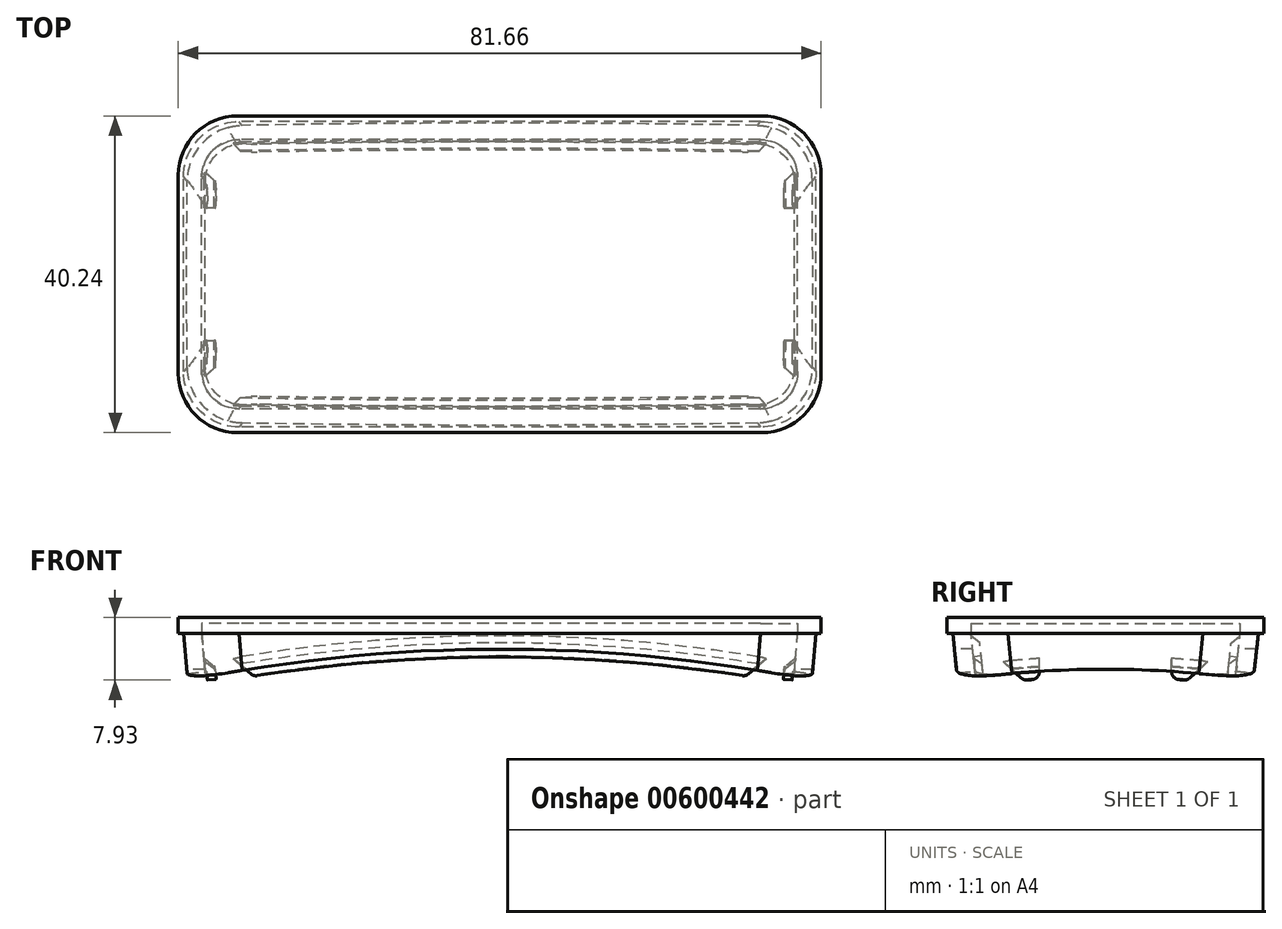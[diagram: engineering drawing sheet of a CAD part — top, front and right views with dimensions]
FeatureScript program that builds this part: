
annotation { "Feature Type Name" : "Feature", "Feature Type Description" : "" }
export const myFeature = defineFeature(function(context is Context, id is Id, definition is map)
    precondition{}
    {
        {
            var Q0;
            Q0=qCreatedBy(makeId("Top.planeOp"),FACE);
            var sketch = newSketch(context, id + "F0", { "sketchPlane" : qUnion([Q0])});
            skLineSegment(sketch, "E0.bottom", {"start": v(-32.64, 18.78) * mm, "end": v(32.64, 18.78) * mm});
            skLineSegment(sketch, "E0.top", {"start": v(-32.64, -18.78) * mm, "end": v(32.64, -18.78) * mm});
            skLineSegment(sketch, "E0.left", {"start": v(-39.64, 11.78) * mm, "end": v(-39.64, -11.78) * mm});
            skLineSegment(sketch, "E0.right", {"start": v(39.64, 11.78) * mm, "end": v(39.64, -11.78) * mm});
            skPoint(sketch, "E0.middle", {"position": v(0, 0) * mm});
            skPoint(sketch, "E1.visualSharp", {"position": v(-39.64, 18.78) * mm});
            skArc(sketch, "E1.filletArc", {"start": v(-32.64, 18.78) * mm, "mid": v(-37.59, 16.73) * mm, "end": v(-39.64, 11.78) * mm});
            skPoint(sketch, "E2.visualSharp", {"position": v(39.64, 18.78) * mm});
            skArc(sketch, "E2.filletArc", {"start": v(39.64, 11.78) * mm, "mid": v(37.59, 16.73) * mm, "end": v(32.64, 18.78) * mm});
            skPoint(sketch, "E3.visualSharp", {"position": v(39.64, -18.78) * mm});
            skArc(sketch, "E3.filletArc", {"start": v(32.64, -18.78) * mm, "mid": v(37.59, -16.73) * mm, "end": v(39.64, -11.78) * mm});
            skPoint(sketch, "E4.visualSharp", {"position": v(-39.64, -18.78) * mm});
            skArc(sketch, "E4.filletArc", {"start": v(-39.64, -11.78) * mm, "mid": v(-37.59, -16.73) * mm, "end": v(-32.64, -18.78) * mm});
            skSolve(sketch);
        }
        {
            var Q0;
            Q0=qCreatedBy(makeId("Top.planeOp"),FACE);
            cPlane(context, id + "F1", {"entities" : qUnion([Q0]), "cplaneType" : CPlaneType.OFFSET, "offset" : 100 * mm, "width" : 150 * mm, "height" : 150 * mm});
        }
        {
            var Q0;
            Q0=qCreatedBy(id+"F1.planeOp",FACE);
            var sketch = newSketch(context, id + "F2", { "sketchPlane" : qUnion([Q0])});
            skLineSegment(sketch, "E5.bottom", {"start": v(-40.98, 29.29) * mm, "end": v(40.98, 29.29) * mm});
            skLineSegment(sketch, "E5.top", {"start": v(-40.98, -29.29) * mm, "end": v(40.98, -29.29) * mm});
            skLineSegment(sketch, "E5.left", {"start": v(-48.38, 21.9) * mm, "end": v(-48.38, -21.9) * mm});
            skLineSegment(sketch, "E5.right", {"start": v(48.38, 21.9) * mm, "end": v(48.38, -21.9) * mm});
            skPoint(sketch, "E5.middle", {"position": v(0, 0) * mm});
            skPoint(sketch, "E6.visualSharp", {"position": v(-48.38, 29.29) * mm});
            skArc(sketch, "E6.filletArc", {"start": v(-40.98, 29.29) * mm, "mid": v(-46.22, 27.12) * mm, "end": v(-48.38, 21.9) * mm});
            skPoint(sketch, "E7.visualSharp", {"position": v(48.38, 29.29) * mm});
            skArc(sketch, "E7.filletArc", {"start": v(48.38, 21.9) * mm, "mid": v(46.22, 27.12) * mm, "end": v(40.98, 29.29) * mm});
            skPoint(sketch, "E8.visualSharp", {"position": v(48.38, -29.3) * mm});
            skArc(sketch, "E8.filletArc", {"start": v(40.98, -29.29) * mm, "mid": v(46.22, -27.12) * mm, "end": v(48.38, -21.9) * mm});
            skPoint(sketch, "E9.visualSharp", {"position": v(-48.38, -29.3) * mm});
            skArc(sketch, "E9.filletArc", {"start": v(-48.38, -21.9) * mm, "mid": v(-46.22, -27.12) * mm, "end": v(-40.98, -29.29) * mm});
            skSolve(sketch);
        }
        {
            var Q0;
            Q0=makeQuery(id+"F0.imprint","IMPRINT",FACE,{"disambiguationData":[TD([[makeQuery(id+"F0.imprint","IMPRINT",EDGE,{"derivedFrom":sQuery(id+"F0.wireOp",EDGE,"E0.bottom")}),-1.0]])]});
            var Q1;
            Q1=makeQuery(id+"F2.imprint","IMPRINT",FACE,{"disambiguationData":[TD([[makeQuery(id+"F2.imprint","IMPRINT",EDGE,{"derivedFrom":sQuery(id+"F2.wireOp",EDGE,"E5.bottom")}),-1.0]])]});
            loft(context, id + "F3", {"sheetProfilesArray" : [{ "sheetProfileEntities" : qUnion([Q0]) }, { "sheetProfileEntities" : qUnion([Q1]) }]});
        }
        {
            var Q0;
            Q0=makeQuery(id+"F3.opLoft","CAP_FACE",FACE,{"disambiguationData":[OSD([makeQuery(id+"F0.imprint","IMPRINT",FACE,{"disambiguationData":[TD([[makeQuery(id+"F0.imprint","IMPRINT",EDGE,{"derivedFrom":sQuery(id+"F0.wireOp",EDGE,"E0.bottom")}),-1.0]])]})])],"isStart":true});
            var Q1;
            Q1=makeQuery(id+"F3.opLoft","CAP_FACE",FACE,{"disambiguationData":[OSD([makeQuery(id+"F2.imprint","IMPRINT",FACE,{"disambiguationData":[TD([[makeQuery(id+"F2.imprint","IMPRINT",EDGE,{"derivedFrom":sQuery(id+"F2.wireOp",EDGE,"E5.bottom")}),-1.0]])]})])],"isStart":true});
            shell(context, id + "F4", {"entities" : qUnion([Q0, Q1]), "thickness" : 2.3 * mm});
        }
        {
            var Q0;
            Q0=qCreatedBy(makeId("Front.planeOp"),FACE);
            var sketch = newSketch(context, id + "F5", { "sketchPlane" : qUnion([Q0])});
            skArc(sketch, "E10", {"start": v(39.64, 0) * mm, "mid": v(0, 3.97) * mm, "end": v(-39.64, 0) * mm});
            skLineSegment(sketch, "E11", {"start": v(-39.64, 0) * mm, "end": v(39.64, 0) * mm});
            skSolve(sketch);
        }
        {
            var Q0;
            Q0 = qSketchRegion(id + "F5", true);
            var Q1;
            Q1=makeQuery(id+"F3.opLoft","SWEPT_FACE",FACE,{"disambiguationData":[OSD([sQuery(id+"F0.wireOp",EDGE,"E0.bottom"),sQuery(id+"F0.wireOp",EDGE,"E1.filletArc"),sQuery(id+"F0.wireOp",EDGE,"E2.filletArc"),sQuery(id+"F2.wireOp",EDGE,"E5.bottom"),sQuery(id+"F2.wireOp",EDGE,"E6.filletArc"),sQuery(id+"F2.wireOp",EDGE,"E7.filletArc")])]});
            var Q2;
            Q2=makeQuery(id+"F3.opLoft","SWEPT_FACE",FACE,{"disambiguationData":[OSD([sQuery(id+"F0.wireOp",EDGE,"E0.top"),sQuery(id+"F0.wireOp",EDGE,"E3.filletArc"),sQuery(id+"F0.wireOp",EDGE,"E4.filletArc"),sQuery(id+"F2.wireOp",EDGE,"E5.top"),sQuery(id+"F2.wireOp",EDGE,"E8.filletArc"),sQuery(id+"F2.wireOp",EDGE,"E9.filletArc")])]});
            extrude(context, id + "F6", {"entities" : qUnion([Q0]), "operationType" : NewBodyOperationType.REMOVE, "endBound" : BoundingType.UP_TO_SURFACE, "oppositeDirection" : true, "depth" : 25 * mm, "endBoundEntityFace" : qUnion([Q1]), "offsetDistance" : 25 * mm, "hasSecondDirection" : true, "secondDirectionBound" : SecondDirectionBoundingType.UP_TO_SURFACE, "secondDirectionOppositeDirection" : false, "secondDirectionDepth" : 25 * mm, "secondDirectionBoundEntityFace" : qUnion([Q2])});
        }
        {
            var Q0;
            Q0=qCreatedBy(makeId("Right.planeOp"),FACE);
            var sketch = newSketch(context, id + "F7", { "sketchPlane" : qUnion([Q0])});
            skArc(sketch, "E12", {"start": v(18.78, 0) * mm, "mid": v(0, 1.42) * mm, "end": v(-18.78, 0) * mm});
            skLineSegment(sketch, "E13", {"start": v(-18.78, 0) * mm, "end": v(18.78, 0) * mm});
            skSolve(sketch);
        }
        {
            var Q0;
            Q0 = qSketchRegion(id + "F7", true);
            var Q1;
            Q1=makeQuery(id+"F3.opLoft","SWEPT_FACE",FACE,{"disambiguationData":[OSD([sQuery(id+"F0.wireOp",EDGE,"E0.right"),sQuery(id+"F0.wireOp",EDGE,"E2.filletArc"),sQuery(id+"F0.wireOp",EDGE,"E3.filletArc"),sQuery(id+"F2.wireOp",EDGE,"E5.right"),sQuery(id+"F2.wireOp",EDGE,"E7.filletArc"),sQuery(id+"F2.wireOp",EDGE,"E8.filletArc")])]});
            var Q2;
            Q2=makeQuery(id+"F3.opLoft","SWEPT_FACE",FACE,{"disambiguationData":[OSD([sQuery(id+"F0.wireOp",EDGE,"E0.left"),sQuery(id+"F0.wireOp",EDGE,"E1.filletArc"),sQuery(id+"F0.wireOp",EDGE,"E4.filletArc"),sQuery(id+"F2.wireOp",EDGE,"E5.left"),sQuery(id+"F2.wireOp",EDGE,"E6.filletArc"),sQuery(id+"F2.wireOp",EDGE,"E9.filletArc")])]});
            extrude(context, id + "F8", {"entities" : qUnion([Q0]), "operationType" : NewBodyOperationType.REMOVE, "endBound" : BoundingType.UP_TO_SURFACE, "depth" : 25 * mm, "endBoundEntityFace" : qUnion([Q1]), "offsetDistance" : 25 * mm, "hasSecondDirection" : true, "secondDirectionBound" : SecondDirectionBoundingType.UP_TO_SURFACE, "secondDirectionOppositeDirection" : true, "secondDirectionDepth" : 25 * mm, "secondDirectionBoundEntityFace" : qUnion([Q2])});
        }
        {
            var Q0;
            Q0=makeQuery(id+"F8.boolean.opBoolean","INTERSECT",EDGE,{"disambiguationData":[OD(2.0)],"derivedFrom":[makeQuery(id+"F6.boolean.opBoolean","COPY",FACE,{"derivedFrom":makeQuery(id+"F6.opExtrude","SWEPT_FACE",FACE,{"disambiguationData":[OSD([sQuery(id+"F5.wireOp",EDGE,"E10")])]})}),makeQuery(id+"F8.opExtrude","SWEPT_FACE",FACE,{"disambiguationData":[OSD([sQuery(id+"F7.wireOp",EDGE,"E12")])]})]});
            var Q1;
            Q1=makeQuery(id+"F8.boolean.opBoolean","INTERSECT",EDGE,{"disambiguationData":[OD(3.0)],"derivedFrom":[makeQuery(id+"F6.boolean.opBoolean","COPY",FACE,{"derivedFrom":makeQuery(id+"F6.opExtrude","SWEPT_FACE",FACE,{"disambiguationData":[OSD([sQuery(id+"F5.wireOp",EDGE,"E10")])]})}),makeQuery(id+"F8.opExtrude","SWEPT_FACE",FACE,{"disambiguationData":[OSD([sQuery(id+"F7.wireOp",EDGE,"E12")])]})]});
            var Q2;
            Q2=makeQuery(id+"F8.boolean.opBoolean","INTERSECT",EDGE,{"disambiguationData":[OD(0.0)],"derivedFrom":[makeQuery(id+"F6.boolean.opBoolean","COPY",FACE,{"derivedFrom":makeQuery(id+"F6.opExtrude","SWEPT_FACE",FACE,{"disambiguationData":[OSD([sQuery(id+"F5.wireOp",EDGE,"E10")])]})}),makeQuery(id+"F8.opExtrude","SWEPT_FACE",FACE,{"disambiguationData":[OSD([sQuery(id+"F7.wireOp",EDGE,"E12")])]})]});
            var Q3;
            Q3=makeQuery(id+"F8.boolean.opBoolean","INTERSECT",EDGE,{"disambiguationData":[OD(1.0)],"derivedFrom":[makeQuery(id+"F6.boolean.opBoolean","COPY",FACE,{"derivedFrom":makeQuery(id+"F6.opExtrude","SWEPT_FACE",FACE,{"disambiguationData":[OSD([sQuery(id+"F5.wireOp",EDGE,"E10")])]})}),makeQuery(id+"F8.opExtrude","SWEPT_FACE",FACE,{"disambiguationData":[OSD([sQuery(id+"F7.wireOp",EDGE,"E12")])]})]});
            fillet(context, id + "F9", {"entities" : qUnion([Q0, Q1, Q2, Q3]), "radius" : 40 * mm, "tangentPropagation" : true, "allowEdgeOverflow" : false});
        }
        {
            var Q0;
            Q0=qCreatedBy(makeId("Front.planeOp"),FACE);
            var sketch = newSketch(context, id + "F10", { "sketchPlane" : qUnion([Q0])});
            skLineSegment(sketch, "E14.bottom", {"start": v(-48.38, 100) * mm, "end": v(48.38, 100) * mm});
            skLineSegment(sketch, "E14.top", {"start": v(-48.38, 7.97) * mm, "end": v(48.38, 7.97) * mm});
            skLineSegment(sketch, "E14.left", {"start": v(-48.38, 100) * mm, "end": v(-48.38, 7.97) * mm});
            skLineSegment(sketch, "E14.right", {"start": v(48.38, 100) * mm, "end": v(48.38, 7.97) * mm});
            skSolve(sketch);
        }
        {
            var Q0;
            Q0 = qSketchRegion(id + "F10", true);
            var Q1;
            Q1=makeQuery(id+"F3.opLoft","SWEPT_FACE",FACE,{"disambiguationData":[OSD([sQuery(id+"F0.wireOp",EDGE,"E0.bottom"),sQuery(id+"F0.wireOp",EDGE,"E1.filletArc"),sQuery(id+"F0.wireOp",EDGE,"E2.filletArc"),sQuery(id+"F2.wireOp",EDGE,"E5.bottom"),sQuery(id+"F2.wireOp",EDGE,"E6.filletArc"),sQuery(id+"F2.wireOp",EDGE,"E7.filletArc")])]});
            var Q2;
            Q2=makeQuery(id+"F3.opLoft","SWEPT_FACE",FACE,{"disambiguationData":[OSD([sQuery(id+"F0.wireOp",EDGE,"E0.top"),sQuery(id+"F0.wireOp",EDGE,"E3.filletArc"),sQuery(id+"F0.wireOp",EDGE,"E4.filletArc"),sQuery(id+"F2.wireOp",EDGE,"E5.top"),sQuery(id+"F2.wireOp",EDGE,"E8.filletArc"),sQuery(id+"F2.wireOp",EDGE,"E9.filletArc")])]});
            extrude(context, id + "F11", {"entities" : qUnion([Q0]), "operationType" : NewBodyOperationType.REMOVE, "endBound" : BoundingType.UP_TO_SURFACE, "oppositeDirection" : true, "depth" : 25 * mm, "endBoundEntityFace" : qUnion([Q1]), "offsetDistance" : 25 * mm, "hasSecondDirection" : true, "secondDirectionBound" : SecondDirectionBoundingType.UP_TO_SURFACE, "secondDirectionOppositeDirection" : false, "secondDirectionDepth" : 25 * mm, "secondDirectionBoundEntityFace" : qUnion([Q2])});
        }
        {
            var Q0;
            Q0=makeQuery(id+"F4.opShell","OFFSET_FACE",FACE,{"disambiguationData":[OSD([sQuery(id+"F0.wireOp",EDGE,"E0.bottom"),sQuery(id+"F0.wireOp",EDGE,"E1.filletArc"),sQuery(id+"F0.wireOp",EDGE,"E2.filletArc"),sQuery(id+"F2.wireOp",EDGE,"E5.bottom"),sQuery(id+"F2.wireOp",EDGE,"E6.filletArc"),sQuery(id+"F2.wireOp",EDGE,"E7.filletArc")])]});
            var sketch = newSketch(context, id + "F12", { "sketchPlane" : qUnion([Q0])});
            skArc(sketch, "E15", {"start": v(32.77, 3.53) * mm, "mid": v(0, 6.2) * mm, "end": v(-32.77, 3.53) * mm});
            skLineSegment(sketch, "E16", {"start": v(31.27, 2.25) * mm, "end": v(32.77, 3.53) * mm});
            skArc(sketch, "E17", {"start": v(31.27, 2.25) * mm, "mid": v(0, 4.7) * mm, "end": v(-31.27, 2.25) * mm});
            skLineSegment(sketch, "E18", {"start": v(0, 6.2) * mm, "end": v(0, 5.7) * mm, "construction": true});
            skLineSegment(sketch, "E19", {"start": v(0, 5.7) * mm, "end": v(0, 4.7) * mm, "construction": true});
            skLineSegment(sketch, "E20", {"start": v(-32.77, 3.53) * mm, "end": v(-31.27, 2.25) * mm});
            skLineSegment(sketch, "E21", {"start": v(32.77, 3.53) * mm, "end": v(31.27, 2.25) * mm});
            skSolve(sketch);
        }
        {
            var Q0;
            Q0 = qSketchRegion(id + "F12", true);
            extrude(context, id + "F13", {"entities" : qUnion([Q0]), "depth" : 1 * mm, "offsetDistance" : 25 * mm});
        }
        {
            var Q0;
            Q0=makeQuery(id+"F13.opExtrude","SWEPT_BODY",BODY,{"disambiguationData":[OSD([sQuery(id+"F12.wireOp",EDGE,"E15"),sQuery(id+"F12.wireOp",EDGE,"E17"),sQuery(id+"F12.wireOp",EDGE,"E20"),sQuery(id+"F12.wireOp",EDGE,"E21")])]});
            var Q1;
            Q1=qCreatedBy(makeId("Front.planeOp"),FACE);
            mirror(context, id + "F14", {"operationType" : NewBodyOperationType.ADD, "entities" : qUnion([Q0]), "mirrorPlane" : qUnion([Q1])});
        }
        {
            var Q0;
            Q0=makeQuery(id+"F4.opShell","OFFSET_FACE",FACE,{"disambiguationData":[OSD([sQuery(id+"F0.wireOp",EDGE,"E0.left"),sQuery(id+"F0.wireOp",EDGE,"E1.filletArc"),sQuery(id+"F0.wireOp",EDGE,"E4.filletArc"),sQuery(id+"F2.wireOp",EDGE,"E5.left"),sQuery(id+"F2.wireOp",EDGE,"E6.filletArc"),sQuery(id+"F2.wireOp",EDGE,"E9.filletArc")])]});
            var sketch = newSketch(context, id + "F15", { "sketchPlane" : qUnion([Q0])});
            skArc(sketch, "E22", {"start": v(11.9, 4.62) * mm, "mid": v(0, 5.18) * mm, "end": v(-11.9, 4.62) * mm});
            skLineSegment(sketch, "E23", {"start": v(0, 4.68) * mm, "end": v(0, 5.18) * mm, "construction": true});
            skLineSegment(sketch, "E24", {"start": v(-11.9, 4.62) * mm, "end": v(-10.4, 3.25) * mm});
            skLineSegment(sketch, "E25", {"start": v(11.9, 4.62) * mm, "end": v(10.4, 3.25) * mm});
            skArc(sketch, "E26", {"start": v(10.4, 3.25) * mm, "mid": v(0, 3.68) * mm, "end": v(-10.4, 3.25) * mm});
            skLineSegment(sketch, "E27", {"start": v(8.4, 3.4) * mm, "end": v(8.4, 4.9) * mm});
            skLineSegment(sketch, "E28", {"start": v(-8.4, 3.4) * mm, "end": v(-8.4, 4.9) * mm});
            skSolve(sketch);
        }
        {
            var Q0;
            {var subQ7=sQuery(id+"F15.wireOp",EDGE,"E26");var subQ9=sQuery(id+"F15.wireOp",EDGE,"E25");var subQ10=makeQuery(id+"F15.imprint","INTERSECT",VERTEX,{"derivedFrom":[subQ9,subQ7]});Q0=makeQuery(id+"F15.imprint","IMPRINT",FACE,{"disambiguationData":[TD([[makeQuery(id+"F15.imprint","IMPRINT",EDGE,{"disambiguationData":[TD([[subQ10,-1.0]])],"derivedFrom":subQ7}),-1.0]])]});}
            var Q1;
            {var subQ0=sQuery(id+"F15.wireOp",EDGE,"E27");var subQ1=sQuery(id+"F15.wireOp",EDGE,"E22");var subQ2=makeQuery(id+"F15.imprint","INTERSECT",VERTEX,{"derivedFrom":[subQ1,subQ0]});Q1=makeQuery(id+"F15.imprint","IMPRINT",FACE,{"disambiguationData":[TD([[makeQuery(id+"F15.imprint","IMPRINT",EDGE,{"disambiguationData":[TD([[subQ2,1.0]])],"derivedFrom":subQ1}),1.0]])]});}
            var Q2;
            {var subQ7=sQuery(id+"F15.wireOp",EDGE,"E26");var subQ9=sQuery(id+"F15.wireOp",EDGE,"E24");var subQ10=makeQuery(id+"F15.imprint","INTERSECT",VERTEX,{"derivedFrom":[subQ9,subQ7]});Q2=makeQuery(id+"F15.imprint","IMPRINT",FACE,{"disambiguationData":[TD([[makeQuery(id+"F15.imprint","IMPRINT",EDGE,{"disambiguationData":[TD([[subQ10,1.0]])],"derivedFrom":subQ7}),-1.0]])]});}
            var Q3;
            {var subQ9=sQuery(id+"F15.wireOp",EDGE,"E28");var subQ11=sQuery(id+"F15.wireOp",EDGE,"E22");var subQ12=makeQuery(id+"F15.imprint","INTERSECT",VERTEX,{"derivedFrom":[subQ11,subQ9]});Q3=makeQuery(id+"F15.imprint","IMPRINT",FACE,{"disambiguationData":[TD([[makeQuery(id+"F15.imprint","IMPRINT",EDGE,{"disambiguationData":[TD([[subQ12,-1.0]])],"derivedFrom":subQ11}),1.0]])]});}
            extrude(context, id + "F16", {"entities" : qUnion([Q0, Q1, Q2, Q3]), "depth" : 1.3 * mm, "offsetDistance" : 25 * mm});
        }
        {
            var Q0;
            Q0=makeQuery(id+"F16.opExtrude","SWEPT_BODY",BODY,{"disambiguationData":[OSD([sQuery(id+"F15.wireOp",EDGE,"E22"),sQuery(id+"F15.wireOp",EDGE,"E24"),sQuery(id+"F15.wireOp",EDGE,"E25"),sQuery(id+"F15.wireOp",EDGE,"E26")])]});
            var Q1;
            Q1=qCreatedBy(makeId("Right.planeOp"),FACE);
            mirror(context, id + "F17", {"operationType" : NewBodyOperationType.ADD, "entities" : qUnion([Q0]), "mirrorPlane" : qUnion([Q1])});
        }
        {
            var Q0;
            Q0=makeQuery(id+"F16.opExtrude","CAP_FACE",FACE,{"disambiguationData":[OSD([sQuery(id+"F15.wireOp",EDGE,"E22"),sQuery(id+"F15.wireOp",EDGE,"E25"),sQuery(id+"F15.wireOp",EDGE,"E26"),sQuery(id+"F15.wireOp",EDGE,"E27")])],"isStart":true});
            var Q1;
            Q1=makeQuery(id+"F16.opExtrude","CAP_FACE",FACE,{"disambiguationData":[OSD([sQuery(id+"F15.wireOp",EDGE,"E22"),sQuery(id+"F15.wireOp",EDGE,"E24"),sQuery(id+"F15.wireOp",EDGE,"E26"),sQuery(id+"F15.wireOp",EDGE,"E28")])],"isStart":true});
            extrude(context, id + "F18", {"entities" : qUnion([Q0, Q1]), "operationType" : NewBodyOperationType.REMOVE, "oppositeDirection" : true, "depth" : .2 * mm, "offsetDistance" : 25 * mm});
        }
        {
            var Q0;
            Q0=makeQuery(id+"F17.opPattern","COPY",FACE,{"derivedFrom":makeQuery(id+"F16.opExtrude","CAP_FACE",FACE,{"disambiguationData":[OSD([sQuery(id+"F15.wireOp",EDGE,"E22"),sQuery(id+"F15.wireOp",EDGE,"E25"),sQuery(id+"F15.wireOp",EDGE,"E26"),sQuery(id+"F15.wireOp",EDGE,"E27")])],"isStart":true}),"instanceName":"1"});
            var Q1;
            Q1=makeQuery(id+"F17.opPattern","COPY",FACE,{"derivedFrom":makeQuery(id+"F16.opExtrude","CAP_FACE",FACE,{"disambiguationData":[OSD([sQuery(id+"F15.wireOp",EDGE,"E22"),sQuery(id+"F15.wireOp",EDGE,"E24"),sQuery(id+"F15.wireOp",EDGE,"E26"),sQuery(id+"F15.wireOp",EDGE,"E28")])],"isStart":true}),"instanceName":"1"});
            extrude(context, id + "F19", {"entities" : qUnion([Q0, Q1]), "operationType" : NewBodyOperationType.REMOVE, "oppositeDirection" : true, "depth" : .2 * mm, "offsetDistance" : 25 * mm});
        }
        {
            var Q0;
            Q0=makeQuery(id+"F16.opExtrude","CAP_EDGE",EDGE,{"disambiguationData":[OSD([sQuery(id+"F15.wireOp",EDGE,"E22")])],"isStart":true});
            var Q1;
            Q1=makeQuery(id+"F13.opExtrude","CAP_EDGE",EDGE,{"disambiguationData":[OSD([sQuery(id+"F12.wireOp",EDGE,"E15")])],"isStart":true});
            var Q2;
            Q2=makeQuery(id+"F17.opPattern","COPY",EDGE,{"derivedFrom":makeQuery(id+"F16.opExtrude","CAP_EDGE",EDGE,{"disambiguationData":[OSD([sQuery(id+"F15.wireOp",EDGE,"E22")])],"isStart":true}),"instanceName":"1"});
            var Q3;
            Q3=makeQuery(id+"F14.opPattern","COPY",EDGE,{"derivedFrom":makeQuery(id+"F13.opExtrude","CAP_EDGE",EDGE,{"disambiguationData":[OSD([sQuery(id+"F12.wireOp",EDGE,"E15")])],"isStart":true}),"instanceName":"1"});
            chamfer(context, id + "F20", {"entities" : qUnion([Q0, Q1, Q2, Q3]), "width" : 1.2 * mm, "tangentPropagation" : true});
        }
        {
            var Q0;
            Q0=makeQuery(id+"F13.opExtrude","SWEPT_EDGE",EDGE,{"disambiguationData":[OSD([sQuery(id+"F12.wireOp",EDGE,"E17"),sQuery(id+"F12.wireOp",EDGE,"E20")])]});
            var Q1;
            Q1=makeQuery(id+"F16.opExtrude","SWEPT_EDGE",EDGE,{"disambiguationData":[OSD([sQuery(id+"F15.wireOp",EDGE,"E25"),sQuery(id+"F15.wireOp",EDGE,"E26")])]});
            var Q2;
            Q2=makeQuery(id+"F13.opExtrude","SWEPT_EDGE",EDGE,{"disambiguationData":[OSD([sQuery(id+"F12.wireOp",EDGE,"E17"),sQuery(id+"F12.wireOp",EDGE,"E21")])]});
            var Q3;
            Q3=makeQuery(id+"F17.opPattern","COPY",EDGE,{"derivedFrom":makeQuery(id+"F16.opExtrude","SWEPT_EDGE",EDGE,{"disambiguationData":[OSD([sQuery(id+"F15.wireOp",EDGE,"E25"),sQuery(id+"F15.wireOp",EDGE,"E26")])]}),"instanceName":"1"});
            var Q4;
            Q4=makeQuery(id+"F17.opPattern","COPY",EDGE,{"derivedFrom":makeQuery(id+"F16.opExtrude","SWEPT_EDGE",EDGE,{"disambiguationData":[OSD([sQuery(id+"F15.wireOp",EDGE,"E24"),sQuery(id+"F15.wireOp",EDGE,"E26")])]}),"instanceName":"1"});
            var Q5;
            Q5=makeQuery(id+"F14.opPattern","COPY",EDGE,{"derivedFrom":makeQuery(id+"F13.opExtrude","SWEPT_EDGE",EDGE,{"disambiguationData":[OSD([sQuery(id+"F12.wireOp",EDGE,"E17"),sQuery(id+"F12.wireOp",EDGE,"E21")])]}),"instanceName":"1"});
            var Q6;
            Q6=makeQuery(id+"F14.opPattern","COPY",EDGE,{"derivedFrom":makeQuery(id+"F13.opExtrude","SWEPT_EDGE",EDGE,{"disambiguationData":[OSD([sQuery(id+"F12.wireOp",EDGE,"E17"),sQuery(id+"F12.wireOp",EDGE,"E20")])]}),"instanceName":"1"});
            var Q7;
            Q7=makeQuery(id+"F16.opExtrude","SWEPT_EDGE",EDGE,{"disambiguationData":[OSD([sQuery(id+"F15.wireOp",EDGE,"E24"),sQuery(id+"F15.wireOp",EDGE,"E26")])]});
            var Q8;
            Q8=makeQuery(id+"F16.opExtrude","SWEPT_EDGE",EDGE,{"disambiguationData":[OSD([sQuery(id+"F15.wireOp",EDGE,"E26"),sQuery(id+"F15.wireOp",EDGE,"E27")])]});
            var Q9;
            Q9=makeQuery(id+"F16.opExtrude","SWEPT_EDGE",EDGE,{"disambiguationData":[OSD([sQuery(id+"F15.wireOp",EDGE,"E26"),sQuery(id+"F15.wireOp",EDGE,"E28")])]});
            var Q10;
            Q10=makeQuery(id+"F17.opPattern","COPY",EDGE,{"derivedFrom":makeQuery(id+"F16.opExtrude","SWEPT_EDGE",EDGE,{"disambiguationData":[OSD([sQuery(id+"F15.wireOp",EDGE,"E26"),sQuery(id+"F15.wireOp",EDGE,"E28")])]}),"instanceName":"1"});
            var Q11;
            Q11=makeQuery(id+"F17.opPattern","COPY",EDGE,{"derivedFrom":makeQuery(id+"F16.opExtrude","SWEPT_EDGE",EDGE,{"disambiguationData":[OSD([sQuery(id+"F15.wireOp",EDGE,"E26"),sQuery(id+"F15.wireOp",EDGE,"E27")])]}),"instanceName":"1"});
            fillet(context, id + "F21", {"entities" : qUnion([Q0, Q1, Q2, Q3, Q4, Q5, Q6, Q7, Q8, Q9, Q10, Q11]), "radius" : 1 * mm, "tangentPropagation" : true, "allowEdgeOverflow" : false});
        }
        {
            var Q0;
            Q0=sQuery(id+"F10.wireOp",EDGE,"E14.top");
            cPlane(context, id + "F22", {"entities" : qUnion([Q0]), "cplaneType" : CPlaneType.LINE_ANGLE, "offset" : 25 * mm, "angle" : 90 * degree, "width" : 150 * mm, "height" : 150 * mm});
        }
        {
            var Q0;
            Q0=qCreatedBy(id+"F22.planeOp",FACE);
            var sketch = newSketch(context, id + "F23", { "sketchPlane" : qUnion([Q0])});
            skLineSegment(sketch, "E29.bottom", {"start": v(-33.3, 20.12) * mm, "end": v(33.3, 20.12) * mm});
            skLineSegment(sketch, "E29.top", {"start": v(-33.3, -20.12) * mm, "end": v(33.3, -20.12) * mm});
            skLineSegment(sketch, "E29.left", {"start": v(-40.83, 12.59) * mm, "end": v(-40.83, -12.59) * mm});
            skLineSegment(sketch, "E29.right", {"start": v(40.83, 12.59) * mm, "end": v(40.83, -12.59) * mm});
            skPoint(sketch, "E29.middle", {"position": v(0, 0) * mm});
            skPoint(sketch, "E30.visualSharp", {"position": v(-40.83, 20.12) * mm});
            skArc(sketch, "E30.filletArc", {"start": v(-33.3, 20.12) * mm, "mid": v(-38.63, 17.91) * mm, "end": v(-40.83, 12.59) * mm});
            skPoint(sketch, "E31.visualSharp", {"position": v(40.83, 20.12) * mm});
            skArc(sketch, "E31.filletArc", {"start": v(40.83, 12.59) * mm, "mid": v(38.63, 17.91) * mm, "end": v(33.3, 20.12) * mm});
            skPoint(sketch, "E32.visualSharp", {"position": v(40.83, -20.12) * mm});
            skArc(sketch, "E32.filletArc", {"start": v(33.3, -20.12) * mm, "mid": v(38.63, -17.91) * mm, "end": v(40.83, -12.59) * mm});
            skPoint(sketch, "E33.visualSharp", {"position": v(-40.83, -20.12) * mm});
            skArc(sketch, "E33.filletArc", {"start": v(-40.83, -12.59) * mm, "mid": v(-38.63, -17.91) * mm, "end": v(-33.3, -20.12) * mm});
            skLineSegment(sketch, "E34", {"start": v(-40.33, 0) * mm, "end": v(-40.83, 0) * mm, "construction": true});
            skLineSegment(sketch, "E35", {"start": v(0, 20.12) * mm, "end": v(0, 19.62) * mm, "construction": true});
            skLineSegment(sketch, "E36", {"start": v(-40.33, -12.59) * mm, "end": v(-33.3, -12.59) * mm, "construction": true});
            skLineSegment(sketch, "E37", {"start": v(-33.3, -12.59) * mm, "end": v(-33.3, -19.62) * mm, "construction": true});
            skSolve(sketch);
        }
        {
            var Q0;
            Q0 = qSketchRegion(id + "F23", true);
            extrude(context, id + "F24", {"entities" : qUnion([Q0]), "operationType" : NewBodyOperationType.ADD, "oppositeDirection" : true, "depth" : 2 * mm, "offsetDistance" : 25 * mm});
        }
        {
            var Q0;
            {var subQ6=sQuery(id+"F2.wireOp",EDGE,"E7.filletArc");var subQ8=sQuery(id+"F2.wireOp",EDGE,"E5.bottom");var subQ9=sQuery(id+"F0.wireOp",EDGE,"E2.filletArc");var subQ11=sQuery(id+"F0.wireOp",EDGE,"E0.bottom");var subQ12=sQuery(id+"F2.wireOp",EDGE,"E6.filletArc");var subQ14=sQuery(id+"F0.wireOp",EDGE,"E1.filletArc");Q0=makeQuery(id+"F24.boolean.opBoolean","SPLIT",FACE,{"disambiguationData":[TD([makeQuery(id+"F4.opShell","OFFSET_FACE",FACE,{"disambiguationData":[OSD([subQ11,subQ14,subQ9,subQ8,subQ12,subQ6])]})])],"derivedFrom":makeQuery(id+"F24.opExtrude","CAP_FACE",FACE,{"disambiguationData":[OSD([sQuery(id+"F23.wireOp",EDGE,"E29.bottom"),sQuery(id+"F23.wireOp",EDGE,"E29.top"),sQuery(id+"F23.wireOp",EDGE,"E29.left"),sQuery(id+"F23.wireOp",EDGE,"E29.right"),sQuery(id+"F23.wireOp",EDGE,"E30.filletArc"),sQuery(id+"F23.wireOp",EDGE,"E31.filletArc"),sQuery(id+"F23.wireOp",EDGE,"E32.filletArc"),sQuery(id+"F23.wireOp",EDGE,"E33.filletArc")])],"isStart":false})});}
            extrude(context, id + "F25", {"entities" : qUnion([Q0]), "operationType" : NewBodyOperationType.REMOVE, "oppositeDirection" : true, "depth" : 1.25 * mm, "offsetDistance" : 25 * mm});
        }
    });
